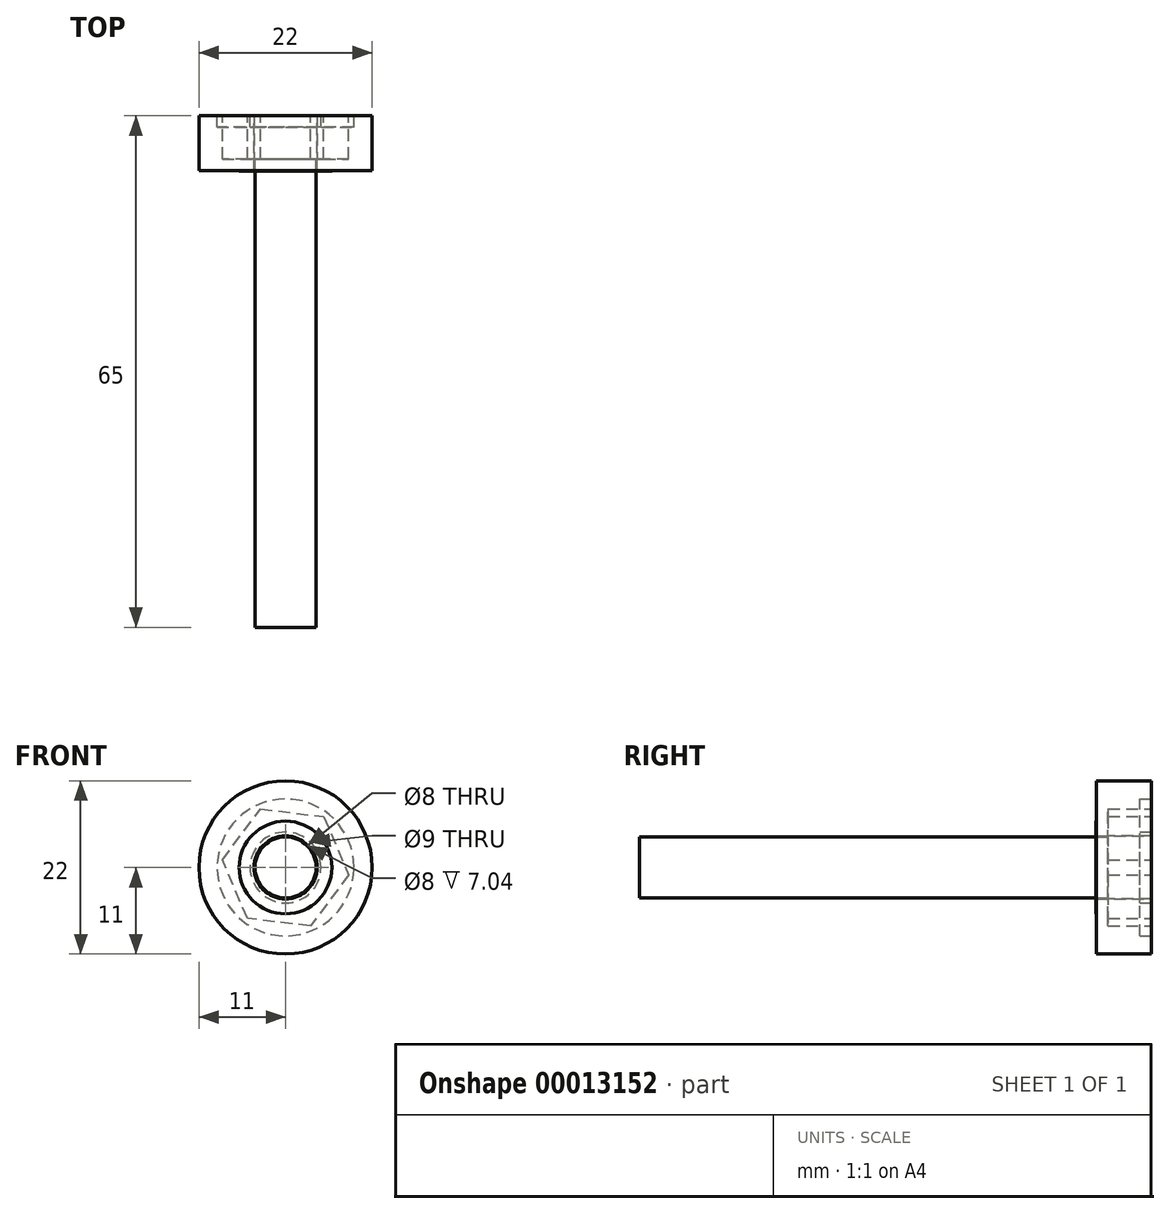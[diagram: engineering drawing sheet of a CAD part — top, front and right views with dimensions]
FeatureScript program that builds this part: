
annotation { "Feature Type Name" : "Feature", "Feature Type Description" : "" }
export const myFeature = defineFeature(function(context is Context, id is Id, definition is map)
    precondition{}
    {
        {
            var Q0;
            Q0=qCreatedBy(makeId("Front.planeOp"),FACE);
            var sketch = newSketch(context, id + "F0", { "sketchPlane" : qUnion([Q0])});
            skCircle(sketch, "E0", {"center": v(0, 0) * mm, "radius": 11 * mm});
            skCircle(sketch, "E1", {"center": v(0, 0) * mm, "radius": 4 * mm});
            skCircle(sketch, "E2.0", {"center": v(0, 0) * mm, "radius": 5.9 * mm});
            skSolve(sketch);
        }
        {
            var Q0;
            Q0=makeQuery(id+"F0.imprint","IMPRINT",FACE,{"disambiguationData":[TD([[makeQuery(id+"F0.imprint","IMPRINT",EDGE,{"derivedFrom":sQuery(id+"F0.wireOp",EDGE,"E0")}),1.0]])]});
            extrude(context, id + "F1", {"entities" : qUnion([Q0]), "depth" : 6.97 * mm});
        }
        {
            var Q0;
            Q0=makeQuery(id+"F0.imprint","IMPRINT",FACE,{"disambiguationData":[TD([[makeQuery(id+"F0.imprint","IMPRINT",EDGE,{"derivedFrom":sQuery(id+"F0.wireOp",EDGE,"E1")}),-1.0]])]});
            extrude(context, id + "F2", {"entities" : qUnion([Q0]), "depth" : 7.04 * mm});
        }
        {
            var Q0;
            Q0=qCreatedBy(makeId("Front.planeOp"),FACE);
            var sketch = newSketch(context, id + "F3", { "sketchPlane" : qUnion([Q0])});
            skCircle(sketch, "E3.cCircle", {"center": v(0, 0) * mm, "radius": 6.88 * mm, "construction": true});
            skLineSegment(sketch, "E3.0", {"start": v(7.75, 1.73) * mm, "end": v(5.37, -5.84) * mm});
            skLineSegment(sketch, "E3.1", {"start": v(5.37, -5.84) * mm, "end": v(-2.38, -7.57) * mm});
            skLineSegment(sketch, "E3.2", {"start": v(-2.38, -7.57) * mm, "end": v(-7.75, -1.73) * mm});
            skLineSegment(sketch, "E3.3", {"start": v(-7.75, -1.73) * mm, "end": v(-5.37, 5.84) * mm});
            skLineSegment(sketch, "E3.4", {"start": v(-5.37, 5.84) * mm, "end": v(2.38, 7.57) * mm});
            skLineSegment(sketch, "E3.5", {"start": v(2.38, 7.57) * mm, "end": v(7.75, 1.73) * mm});
            skPoint(sketch, "E3.0.midPoint", {"position": v(6.56, -2.06) * mm});
            skCircle(sketch, "E4", {"center": v(0, 0) * mm, "radius": 3.88 * mm});
            skSolve(sketch);
        }
        {
            var Q0;
            Q0=makeQuery(id+"F3.imprint","IMPRINT",FACE,{"disambiguationData":[TD([[makeQuery(id+"F3.imprint","IMPRINT",EDGE,{"derivedFrom":sQuery(id+"F3.wireOp",EDGE,"E4")}),1.0]])]});
            extrude(context, id + "F4", {"entities" : qUnion([Q0]), "depth" : 65 * mm});
        }
        {
            var Q0;
            Q0=qSketchRegion(id+"F3",true);
            extrude(context, id + "F5", {"entities" : qUnion([Q0]), "operationType" : NewBodyOperationType.ADD, "depth" : 4.75 * mm});
        }
        {
            var Q0;
            Q0=qCreatedBy(makeId("Front.planeOp"),FACE);
            var sketch = newSketch(context, id + "F6", { "sketchPlane" : qUnion([Q0])});
            skCircle(sketch, "E5", {"center": v(0, 0) * mm, "radius": 8.7 * mm});
            skCircle(sketch, "E6", {"center": v(0, 0) * mm, "radius": 4.5 * mm});
            skSolve(sketch);
        }
        {
            var Q0;
            Q0=qSketchRegion(id+"F6",true);
            extrude(context, id + "F7", {"entities" : qUnion([Q0]), "depth" : 1.45 * mm});
        }
        {
            var Q0;
            Q0=qCreatedBy(makeId("Front.planeOp"),FACE);
            var sketch = newSketch(context, id + "F8", { "sketchPlane" : qUnion([Q0])});
            skCircle(sketch, "E7.cCircle", {"center": v(0, 0) * mm, "radius": 7 * mm, "construction": true});
            skLineSegment(sketch, "E7.0", {"start": v(8.02, -0.97) * mm, "end": v(3.18, -7.43) * mm});
            skLineSegment(sketch, "E7.1", {"start": v(3.18, -7.43) * mm, "end": v(-4.85, -6.47) * mm});
            skLineSegment(sketch, "E7.2", {"start": v(-4.85, -6.47) * mm, "end": v(-8.02, 0.97) * mm});
            skLineSegment(sketch, "E7.3", {"start": v(-8.02, 0.97) * mm, "end": v(-3.18, 7.43) * mm});
            skLineSegment(sketch, "E7.4", {"start": v(-3.18, 7.43) * mm, "end": v(4.85, 6.47) * mm});
            skLineSegment(sketch, "E7.5", {"start": v(4.85, 6.47) * mm, "end": v(8.02, -0.97) * mm});
            skPoint(sketch, "E7.0.midPoint", {"position": v(5.6, -4.2) * mm});
            skSolve(sketch);
        }
        {
            var Q0;
            Q0=makeQuery(id+"F8.imprint","IMPRINT",FACE,{"disambiguationData":[TD([[makeQuery(id+"F8.imprint","IMPRINT",EDGE,{"derivedFrom":sQuery(id+"F8.wireOp",EDGE,"E7.0")}),-1.0]])]});
            extrude(context, id + "F9", {"entities" : qUnion([Q0]), "depth" : 5.5 * mm});
        }
        {
            var Q0;
            Q0=makeQuery(id+"F9.opExtrude","CAP_FACE",FACE,{"disambiguationData":[OSD([sQuery(id+"F8.wireOp",EDGE,"E7.0"),sQuery(id+"F8.wireOp",EDGE,"E7.1"),sQuery(id+"F8.wireOp",EDGE,"E7.2"),sQuery(id+"F8.wireOp",EDGE,"E7.3"),sQuery(id+"F8.wireOp",EDGE,"E7.4"),sQuery(id+"F8.wireOp",EDGE,"E7.5")])],"isStart":false});
            var sketch = newSketch(context, id + "F10", { "sketchPlane" : qUnion([Q0])});
            skCircle(sketch, "E8", {"center": v(0, 0) * mm, "radius": 4 * mm});
            skSolve(sketch);
        }
        {
            var Q0;
            Q0=makeQuery(id+"F10.imprint","IMPRINT",FACE,{"disambiguationData":[TD([[makeQuery(id+"F10.imprint","IMPRINT",EDGE,{"derivedFrom":sQuery(id+"F10.wireOp",EDGE,"E8")}),1.0]])]});
            var Q1;
            Q1=sQuery(id+"F10.wireOp",EDGE,"E8");
            extrude(context, id + "F11", {"entities" : qUnion([Q0]), "operationType" : NewBodyOperationType.REMOVE, "surfaceEntities" : qUnion([Q1]), "oppositeDirection" : true, "depth" : 25 * mm});
        }
    });
